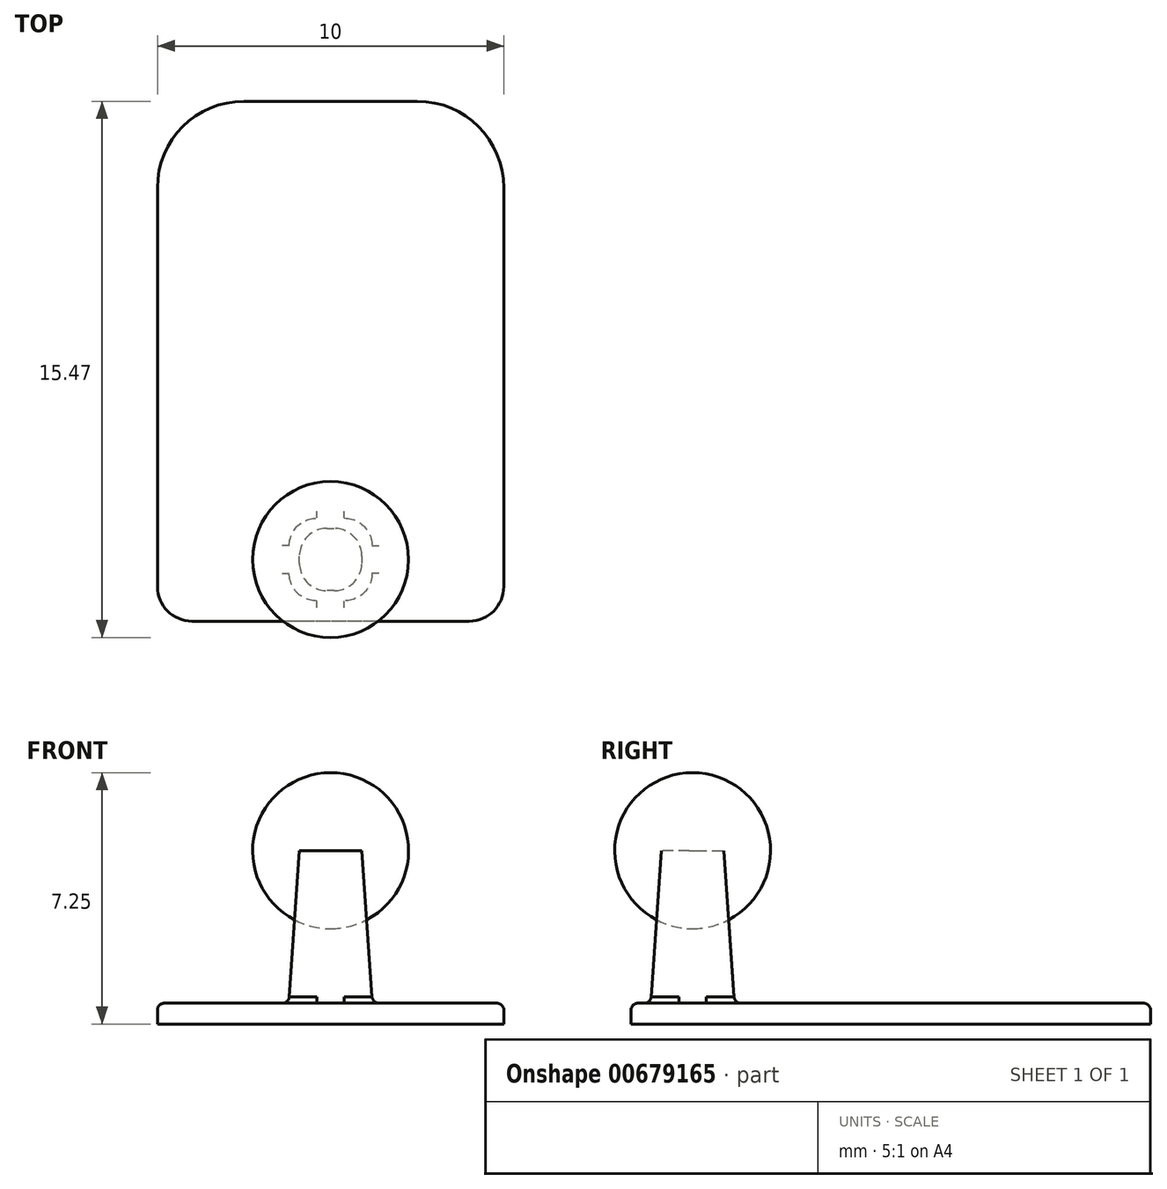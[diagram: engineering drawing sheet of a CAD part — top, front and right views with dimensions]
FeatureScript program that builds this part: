
annotation { "Feature Type Name" : "Feature", "Feature Type Description" : "" }
export const myFeature = defineFeature(function(context is Context, id is Id, definition is map)
    precondition{}
    {
        {
            var Q0;
            Q0=qCreatedBy(makeId("Top.planeOp"),FACE);
            var sketch = newSketch(context, id + "F0", { "sketchPlane" : qUnion([Q0])});
            skLineSegment(sketch, "E0.bottom", {"start": v(4, -7.5) * mm, "end": v(-4, -7.5) * mm});
            skLineSegment(sketch, "E0.top", {"start": v(2.5, 7.5) * mm, "end": v(-2.5, 7.5) * mm});
            skLineSegment(sketch, "E0.left", {"start": v(5, -6.5) * mm, "end": v(5, 5) * mm});
            skLineSegment(sketch, "E0.right", {"start": v(-5, -6.5) * mm, "end": v(-5, 5) * mm});
            skPoint(sketch, "E0.middle", {"position": v(0, 0) * mm});
            skPoint(sketch, "E1.visualSharp", {"position": v(-5, 7.5) * mm});
            skArc(sketch, "E1.filletArc", {"start": v(-2.5, 7.5) * mm, "mid": v(-4.27, 6.77) * mm, "end": v(-5, 5) * mm});
            skPoint(sketch, "E2.visualSharp", {"position": v(5, 7.5) * mm});
            skArc(sketch, "E2.filletArc", {"start": v(5, 5) * mm, "mid": v(4.27, 6.77) * mm, "end": v(2.5, 7.5) * mm});
            skPoint(sketch, "E3.visualSharp", {"position": v(-5, -7.5) * mm});
            skArc(sketch, "E3.filletArc", {"start": v(-5, -6.5) * mm, "mid": v(-4.7, -7.2) * mm, "end": v(-4, -7.5) * mm});
            skPoint(sketch, "E4.visualSharp", {"position": v(5, -7.5) * mm});
            skArc(sketch, "E4.filletArc", {"start": v(4, -7.5) * mm, "mid": v(4.7, -7.2) * mm, "end": v(5, -6.5) * mm});
            skLineSegment(sketch, "E5.bottom", {"start": v(-1.25, -4.47) * mm, "end": v(1.25, -4.47) * mm});
            skLineSegment(sketch, "E5.top", {"start": v(-1.25, -6.97) * mm, "end": v(1.25, -6.97) * mm});
            skLineSegment(sketch, "E5.left", {"start": v(-1.25, -4.47) * mm, "end": v(-1.25, -6.97) * mm});
            skLineSegment(sketch, "E5.right", {"start": v(1.25, -4.47) * mm, "end": v(1.25, -6.97) * mm});
            skCircle(sketch, "E6", {"center": v(-27.51, -9.68) * mm, "radius": 2.25 * mm});
            skSolve(sketch);
        }
        {
            var Q0;
            Q0=makeQuery(id+"F0.imprint","IMPRINT",FACE,{"disambiguationData":[TD([[makeQuery(id+"F0.imprint","IMPRINT",EDGE,{"derivedFrom":sQuery(id+"F0.wireOp",EDGE,"E0.bottom")}),-1.0]])]});
            var Q1;
            Q1=makeQuery(id+"F0.imprint","IMPRINT",FACE,{"disambiguationData":[TD([[makeQuery(id+"F0.imprint","IMPRINT",EDGE,{"derivedFrom":sQuery(id+"F0.wireOp",EDGE,"E5.bottom")}),-1.0]])]});
            extrude(context, id + "F1", {"entities" : qUnion([Q0, Q1]), "depth" : 0.6 * mm, "offsetDistance" : 25 * mm});
        }
        {
            var Q0;
            Q0=makeQuery(id+"F0.imprint","IMPRINT",FACE,{"disambiguationData":[TD([[makeQuery(id+"F0.imprint","IMPRINT",EDGE,{"derivedFrom":sQuery(id+"F0.wireOp",EDGE,"E5.bottom")}),-1.0]])]});
            extrude(context, id + "F2", {"entities" : qUnion([Q0]), "operationType" : NewBodyOperationType.ADD, "depth" : 5 * mm, "offsetDistance" : 25 * mm, "hasDraft" : true, "draftAngle" : 4 * degree, "draftPullDirection" : true});
        }
        {
            var Q0;
            Q0=makeQuery(id+"F2.opExtrude","CAP_FACE",FACE,{"disambiguationData":[OSD([sQuery(id+"F0.wireOp",EDGE,"E5.bottom"),sQuery(id+"F0.wireOp",EDGE,"E5.top"),sQuery(id+"F0.wireOp",EDGE,"E5.left"),sQuery(id+"F0.wireOp",EDGE,"E5.right")])],"isStart":false});
            var sketch = newSketch(context, id + "F3", { "sketchPlane" : qUnion([Q0])});
            skCircle(sketch, "E7", {"center": v(0, -5.72) * mm, "radius": 2.25 * mm});
            skPoint(sketch, "E7.centerSnap0", {"position": v(-0.9, -5.72) * mm});
            skSolve(sketch);
        }
        {
            var Q0;
            Q0=makeQuery(id+"F3.imprint","IMPRINT",FACE,{"disambiguationData":[TD([[makeQuery(id+"F3.imprint","IMPRINT",EDGE,{"derivedFrom":sQuery(id+"F3.wireOp",EDGE,"E7")}),1.0]])]});
            var Q1;
            Q1=makeQuery(id+"F3.imprint","IMPRINT",FACE,{"disambiguationData":[TD([[makeQuery(id+"F3.imprint","IMPRINT",EDGE,{"derivedFrom":makeQuery(id+"F2.opExtrude","CAP_EDGE",EDGE,{"disambiguationData":[OSD([sQuery(id+"F0.wireOp",EDGE,"E5.bottom")])],"isStart":false})}),-1.0]])]});
            extrude(context, id + "F4", {"entities" : qUnion([Q0, Q1]), "endBound" : BoundingType.SYMMETRIC, "depth" : 4.5 * mm, "offsetDistance" : 25 * mm});
        }
        {
            var Q0;
            Q0=makeQuery(id+"F4.opExtrude","CAP_FACE",FACE,{"disambiguationData":[OSD([sQuery(id+"F3.wireOp",EDGE,"E7")])],"isStart":false});
            var Q1;
            Q1=makeQuery(id+"F4.opExtrude","CAP_FACE",FACE,{"disambiguationData":[OSD([sQuery(id+"F3.wireOp",EDGE,"E7")])],"isStart":true});
            fillet(context, id + "F5", {"entities" : qUnion([Q0, Q1]), "radius" : 2.25 * mm, "tangentPropagation" : true, "allowEdgeOverflow" : false});
        }
        {
            var Q0;
            Q0=makeQuery(id+"F2.opExtrude","SWEPT_EDGE",EDGE,{"disambiguationData":[OSD([sQuery(id+"F0.wireOp",EDGE,"E5.bottom"),sQuery(id+"F0.wireOp",EDGE,"E5.left")])]});
            var Q1;
            Q1=makeQuery(id+"F2.opExtrude","SWEPT_EDGE",EDGE,{"disambiguationData":[OSD([sQuery(id+"F0.wireOp",EDGE,"E5.bottom"),sQuery(id+"F0.wireOp",EDGE,"E5.right")])]});
            var Q2;
            Q2=makeQuery(id+"F2.opExtrude","SWEPT_EDGE",EDGE,{"disambiguationData":[OSD([sQuery(id+"F0.wireOp",EDGE,"E5.top"),sQuery(id+"F0.wireOp",EDGE,"E5.right")])]});
            var Q3;
            Q3=makeQuery(id+"F2.opExtrude","SWEPT_EDGE",EDGE,{"disambiguationData":[OSD([sQuery(id+"F0.wireOp",EDGE,"E5.top"),sQuery(id+"F0.wireOp",EDGE,"E5.left")])]});
            fillet(context, id + "F6", {"entities" : qUnion([Q0, Q1, Q2, Q3]), "radius" : 0.8 * mm, "tangentPropagation" : true, "allowEdgeOverflow" : false});
        }
        {
            var Q0;
            Q0=makeQuery(id+"F1.opExtrude","CAP_FACE",FACE,{"disambiguationData":[OSD([sQuery(id+"F0.wireOp",EDGE,"E0.bottom"),sQuery(id+"F0.wireOp",EDGE,"E0.top"),sQuery(id+"F0.wireOp",EDGE,"E0.left"),sQuery(id+"F0.wireOp",EDGE,"E0.right"),sQuery(id+"F0.wireOp",EDGE,"E1.filletArc"),sQuery(id+"F0.wireOp",EDGE,"E2.filletArc"),sQuery(id+"F0.wireOp",EDGE,"E3.filletArc"),sQuery(id+"F0.wireOp",EDGE,"E4.filletArc")])],"isStart":false});
            fillet(context, id + "F7", {"entities" : qUnion([Q0]), "radius" : 0.2 * mm, "tangentPropagation" : true, "allowEdgeOverflow" : false});
        }
    });
